# Revit family: Stella Steel Post Straight
name_source: partatom
category: Furniture
units: mm (PartAtom-declared; Revit-internal decimal feet)

## family parameters
Always vertical = Yes
Cut with Voids When Loaded = No
OmniClass Number = 23.21.23.13.15
Room Calculation Point = No
Shared = No
Work Plane-Based = No

## types (2) — shared parameters
BIMobject category = bicycle-storage
Body material = Hags - Steel - Powder coated - Black
Body material_90 = Hags - Steel - Powder coated - Black
Construction material = Hags - Steel - Galvanized
Description = Stella Steel Post Straight Tin Roof
Edition number = 1
IFC Classification = Furniture
Manufacturer = Hags
Manufacturer name = HAGS
Model = 8043673
OmniClass Code = 23-21 23 13 15
Product Guid = 90e49432-c870-4a59-897e-b15016e8f9bd
Product name = Capella Steel Post Vaulted Tin Roof Galvanized -Sunken Foundation
Product url = https://www.hags.com
URL = https://www.hags.com
Uniclass 1.4 Code = L8211
Uniclass 1.4 Description = Furniture
zero-valued in all types: Default Elevation

## per-type parameters (varying)
| type | Roof |
| 8043673 Stella Steel Post Straight Tin Roof  Black Galvanized | Hags - Steel - Powder coated - Black |
| 8043675 Stella Steel Post Straight Plastic Roof  Black Galvanized | Plastic |

## geometry (parser evidence)
native form markers: Sweep x3
no freeform markers — native parametric forms only
